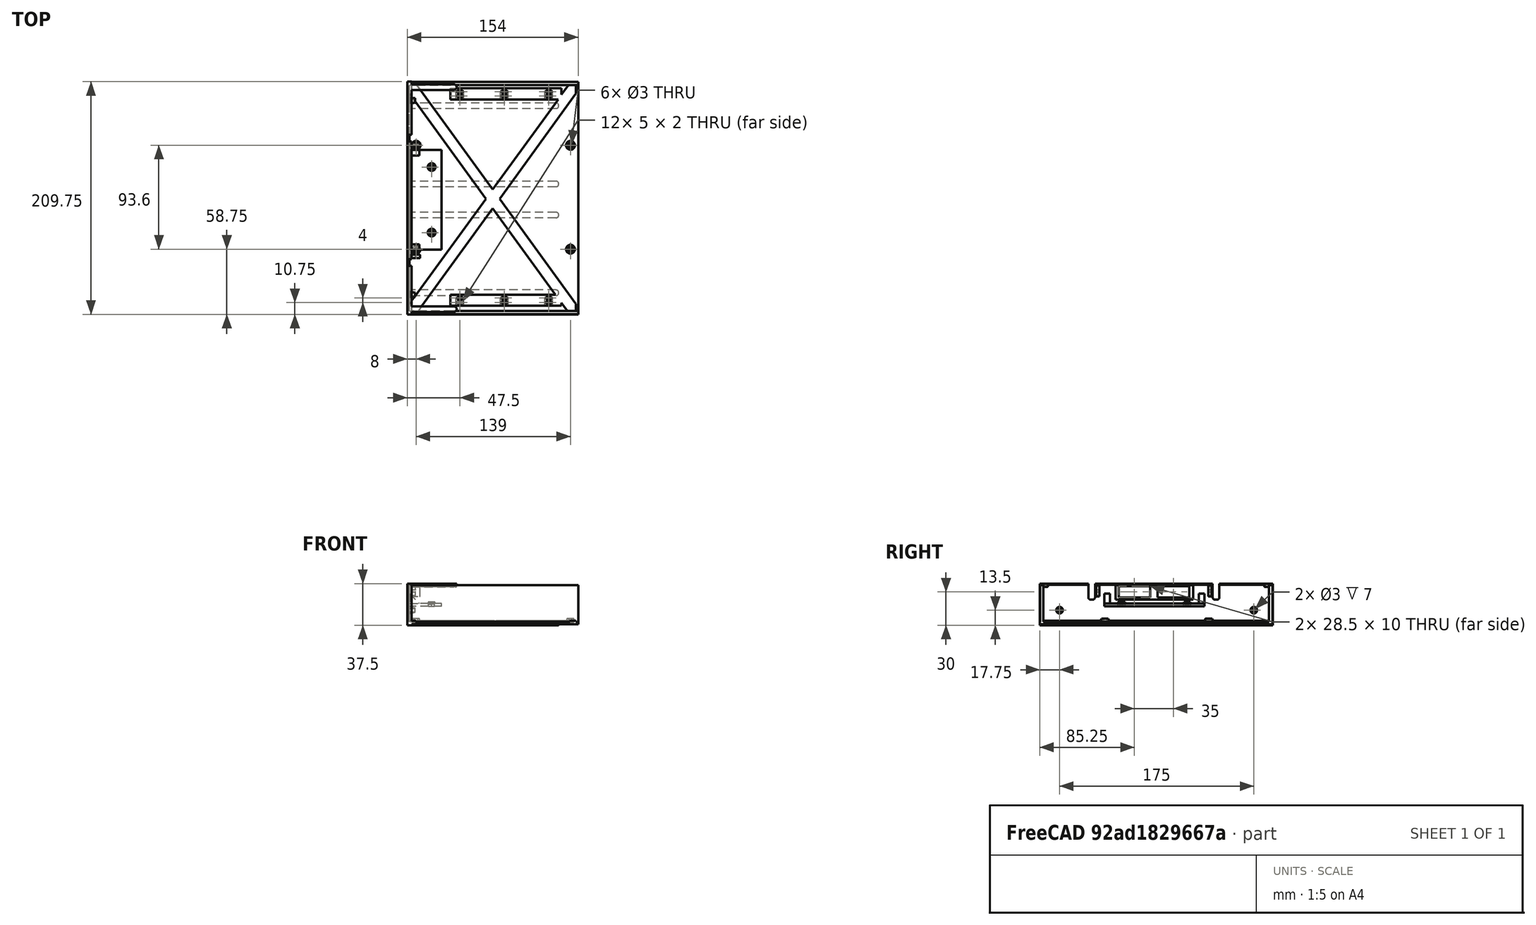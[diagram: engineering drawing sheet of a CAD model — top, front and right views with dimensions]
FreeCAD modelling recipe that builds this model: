
FCSTD DOCUMENT  (FreeCAD 0.19R24291 (Git))
Label: SBC61_tray_wider
License: All rights reserved
LicenseURL: http://en.wikipedia.org/wiki/All_rights_reserved
objects: Part::Box×69, Part::MultiFuse×39, Part::Cylinder×18, Part::Fillet×16, Part::Cut×12, Part::Cone×8, Part::MultiCommon×7, Mesh::Feature×3
note: 169 computed .brp shape members not serialized (recipe doc carries the construction recipe); baked Part::Feature solids carry a one-line shape summary decoded from their .brp

FEATURE [Part::Box] Box  label="Cube"
  AttacherType = Attacher::AttachEngine3D
  Height = 2
  Length = 150
  Placement = pos=(0,-54.75,0) rot=(0,0,1;0rad)
  Width = 209.25
FEATURE [Part::Cylinder] Cylinder
  Angle = 360
  AttacherType = Attacher::AttachEngine3D
  Height = 10
  Placement = pos=(4,4,-1) rot=(0,0,1;0rad)
  Radius = 1.5
FEATURE [Part::Box] Box001  label="Cube001"
  AttacherType = Attacher::AttachEngine3D
  Height = 37.5
  Length = 4
  Placement = pos=(-5,-19.25,-1) rot=(0,0,1;0rad)
  Width = 209.75
FEATURE [Part::Box] Box002  label="Cube002"
  AttacherType = Attacher::AttachEngine3D
  Height = 3
  Length = 130
  Placement = pos=(0,0.75,-2) rot=(0,0,1;0rad)
  Width = 5
FEATURE [Part::Fillet] Fillet
  Base = -> Box002
  Edges = 2 edges r=0.5: [Edge9,Edge11]
FEATURE [Part::Cylinder] Cylinder004
  Angle = 360
  AttacherType = Attacher::AttachEngine3D
  Height = 3
  Placement = pos=(130,3.25,-2) rot=(0,0,-1;0rad)
  Radius = 2.5
FEATURE [Part::Fillet] Fillet001
  Base = -> Cylinder004
  Edges = 1 edges r=0.5: [Edge3]
FEATURE [Part::MultiFuse] Fusion001
  Placement = pos=(0,-38.5,1) rot=(0,0,1;0rad)
  Shapes = -> [Fillet,Fillet001]
FEATURE [Part::Cylinder] Cylinder005
  Angle = 360
  AttacherType = Attacher::AttachEngine3D
  Height = 3
  Placement = pos=(130,3.25,-2) rot=(0,0,-1;0rad)
  Radius = 2.5
FEATURE [Part::Box] Box003  label="Cube003"
  AttacherType = Attacher::AttachEngine3D
  Height = 3
  Length = 130
  Placement = pos=(0,0.75,-2) rot=(0,0,1;0rad)
  Width = 5
FEATURE [Part::Fillet] Fillet002
  Base = -> Box003
  Edges = 2 edges r=0.5: [Edge9,Edge11]
FEATURE [Part::Fillet] Fillet003
  Base = -> Cylinder005
  Edges = 1 edges r=0.5: [Edge3]
FEATURE [Part::MultiFuse] Fusion002
  Placement = pos=(0,130,1) rot=(0,0,1;0rad)
  Shapes = -> [Fillet002,Fillet003]
FEATURE [Part::Cylinder] Cylinder006
  Angle = 360
  AttacherType = Attacher::AttachEngine3D
  Height = 3
  Placement = pos=(130,2.5,-2) rot=(0,0,-1;0rad)
  Radius = 2.5
FEATURE [Part::Box] Box004  label="Cube004"
  AttacherType = Attacher::AttachEngine3D
  Height = 3
  Length = 130
  Placement = pos=(0,0,-2) rot=(0,0,1;0rad)
  Width = 5
FEATURE [Part::Fillet] Fillet004
  Base = -> Box004
  Edges = 2 edges r=0.5: [Edge9,Edge11]
FEATURE [Part::Fillet] Fillet005
  Base = -> Cylinder006
  Edges = 1 edges r=0.5: [Edge3]
FEATURE [Part::MultiFuse] Fusion003
  Placement = pos=(0,60.25,1) rot=(0,0,1;0rad)
  Shapes = -> [Fillet004,Fillet005]
FEATURE [Part::Cylinder] Cylinder007
  Angle = 360
  AttacherType = Attacher::AttachEngine3D
  Height = 3
  Placement = pos=(130,2.5,-2) rot=(0,0,-1;0rad)
  Radius = 2.5
FEATURE [Part::Box] Box005  label="Cube005"
  AttacherType = Attacher::AttachEngine3D
  Height = 3
  Length = 130
  Placement = pos=(0,0,-2) rot=(0,0,1;0rad)
  Width = 5
FEATURE [Part::Fillet] Fillet006
  Base = -> Box005
  Edges = 2 edges r=0.5: [Edge9,Edge11]
FEATURE [Part::Fillet] Fillet007
  Base = -> Cylinder007
  Edges = 1 edges r=0.5: [Edge3]
FEATURE [Part::MultiFuse] Fusion004
  Placement = pos=(0,32.25,1) rot=(0,0,1;0rad)
  Shapes = -> [Fillet006,Fillet007]
FEATURE [Part::Box] Box006  label="Cube006"
  AttacherType = Attacher::AttachEngine3D
  Height = 35.2
  Length = 150
  Placement = pos=(0,-54.5,0) rot=(0,0,1;0rad)
  Width = 3
FEATURE [Part::Box] Box007  label="Cube007"
  AttacherType = Attacher::AttachEngine3D
  Height = 35.2
  Length = 150
  Placement = pos=(0,151.75,0) rot=(0,0,1;0rad)
  Width = 3
FEATURE [Part::Cylinder] Cylinder008
  Angle = 360
  AttacherType = Attacher::AttachEngine3D
  Height = 3
  Placement = pos=(38,3,-2) rot=(0,0,-1;0rad)
  Radius = 2.5
FEATURE [Part::Box] Box008  label="Cube008"
  AttacherType = Attacher::AttachEngine3D
  Height = 3
  Length = 38
  Placement = pos=(0,36.5,-2) rot=(0,0,1;0rad)
  Width = 5
FEATURE [Part::Fillet] Fillet008
  Base = -> Box008
  Edges = 2 edges r=0.5: [Edge9,Edge11]
  Placement = pos=(0,-36,0) rot=(0,0,1;0rad)
FEATURE [Part::Fillet] Fillet009
  Base = -> Cylinder008
  Edges = 1 edges r=0.5: [Edge3]
FEATURE [Part::MultiFuse] Fusion005
  Placement = pos=(0,-53,35.5) rot=(0,0,1;0rad)
  Shapes = -> [Fillet008,Fillet009]
FEATURE [Part::Cylinder] Cylinder009
  Angle = 360
  AttacherType = Attacher::AttachEngine3D
  Height = 3
  Placement = pos=(38,3,-2) rot=(0,0,-1;0rad)
  Radius = 2.5
FEATURE [Part::Box] Box009  label="Cube009"
  AttacherType = Attacher::AttachEngine3D
  Height = 3
  Length = 38
  Placement = pos=(0,0.5,-2) rot=(0,0,1;0rad)
  Width = 5
FEATURE [Part::Fillet] Fillet010
  Base = -> Box009
  Edges = 2 edges r=0.5: [Edge9,Edge11]
FEATURE [Part::Fillet] Fillet011
  Base = -> Cylinder009
  Edges = 1 edges r=0.5: [Edge3]
FEATURE [Part::MultiFuse] Fusion006
  Placement = pos=(0,147,35.5) rot=(0,0,1;0rad)
  Shapes = -> [Fillet010,Fillet011]
FEATURE [Part::Box] Box014  label="Cube014"
  AttacherType = Attacher::AttachEngine3D
  Height = 2
  Length = 5.45
  Placement = pos=(3.25,0,0) rot=(0,0,1;0rad)
  Width = 10
FEATURE [Part::Box] Box015  label="Cube015"
  AttacherType = Attacher::AttachEngine3D
  Height = 2
  Length = 5.45
  Placement = pos=(11.5,4,0) rot=(0,0,1;2.0944rad)
  Width = 10
FEATURE [Part::Box] Box016  label="Cube016"
  AttacherType = Attacher::AttachEngine3D
  Height = 2
  Length = 10
  Placement = pos=(0.55,4,0) rot=(0,0,-1;0.523599rad)
  Width = 5.45
FEATURE [Part::MultiCommon] Common  label="M.25 nut"
  Placement = pos=(-2,0,-1) rot=(0,0,1;0rad)
  Shapes = -> [Box014,Box016,Box015]
FEATURE [Part::Cone] Cone
  Angle = 360
  AttacherType = Attacher::AttachEngine3D
  Height = 3
  Placement = pos=(4,4,2) rot=(0,0,1;0rad)
  Radius1 = 4
  Radius2 = 3
FEATURE [Part::Cone] Cone001
  Angle = 360
  AttacherType = Attacher::AttachEngine3D
  Height = 3
  Placement = pos=(143,4,2) rot=(0,0,1;0rad)
  Radius1 = 4
  Radius2 = 3
FEATURE [Part::Cone] Cone002
  Angle = 360
  AttacherType = Attacher::AttachEngine3D
  Height = 3
  Placement = pos=(4,97.6,2) rot=(0,0,1;0rad)
  Radius1 = 4
  Radius2 = 3
FEATURE [Part::Cone] Cone003
  Angle = 360
  AttacherType = Attacher::AttachEngine3D
  Height = 3
  Placement = pos=(143,97.6,2) rot=(0,0,1;0rad)
  Radius1 = 4
  Radius2 = 3
FEATURE [Part::Box] Box017  label="Cube017"
  AttacherType = Attacher::AttachEngine3D
  Height = 33.5
  Length = 4
  Placement = pos=(-3,-16,2) rot=(0,0,1;0rad)
  Width = 203.25
FEATURE [Part::Cut] Cut  label="Face_plate_full"
  Base = -> Box001
  Placement = pos=(1,-34.5,0) rot=(0,0,1;0rad)
  Tool = -> Box017
FEATURE [Part::Box] Box018  label="Cube018"
  AttacherType = Attacher::AttachEngine3D
  Height = 15
  Length = 10
  Placement = pos=(0,0,16) rot=(0,0,1;0rad)
  Width = 6
FEATURE [Part::Fillet] Fillet012
  Base = -> Box018
  Edges = 2 edges r=2: [Edge9,Edge11]
  Placement = pos=(0,-10,4) rot=(0,0,1;0rad)
FEATURE [Part::Box] Box020  label="Cube020"
  AttacherType = Attacher::AttachEngine3D
  Height = 15
  Length = 10
  Placement = pos=(0,0,16) rot=(0,0,1;0rad)
  Width = 6
FEATURE [Part::Fillet] Fillet014
  Base = -> Box020
  Edges = 2 edges r=2: [Edge9,Edge11]
  Placement = pos=(0,102,4) rot=(0,0,1;0rad)
FEATURE [Part::MultiFuse] Fusion
  Placement = pos=(-5,0,2) rot=(0,0,1;0rad)
  Shapes = -> [Fillet012,Fillet014]
FEATURE [Part::Cut] Cut001  label="Face plate with cuts"
  Base = -> Cut
  Placement = pos=(0,-1,0) rot=(0,0,1;0rad)
  Tool = -> Fusion
FEATURE [Part::MultiFuse] Fusion007  label="Bottom"
  Shapes = -> [Box,Fusion001,Fusion002,Fusion003,Fusion004,Cone,Cone001,Cone002,Cone003]
FEATURE [Part::MultiFuse] Fusion008  label="screw_hole"
  Shapes = -> [Cylinder,Common]
FEATURE [Part::Box] Box021  label="Cube021"
  AttacherType = Attacher::AttachEngine3D
  Height = 2
  Length = 5.45
  Placement = pos=(3.25,0,0) rot=(0,0,1;0rad)
  Width = 10
FEATURE [Part::Box] Box022  label="Cube022"
  AttacherType = Attacher::AttachEngine3D
  Height = 2
  Length = 5.45
  Placement = pos=(11.5,4,0) rot=(0,0,1;2.0944rad)
  Width = 10
FEATURE [Part::Box] Box023  label="Cube023"
  AttacherType = Attacher::AttachEngine3D
  Height = 2
  Length = 10
  Placement = pos=(0.55,4,0) rot=(0,0,-1;0.523599rad)
  Width = 5.45
FEATURE [Part::Cylinder] Cylinder010
  Angle = 360
  AttacherType = Attacher::AttachEngine3D
  Height = 10
  Placement = pos=(4,4,-1) rot=(0,0,1;0rad)
  Radius = 1.5
FEATURE [Part::MultiCommon] Common001  label="M.25 nut001"
  Placement = pos=(-2,0,-1) rot=(0,0,1;0rad)
  Shapes = -> [Box021,Box023,Box022]
FEATURE [Part::MultiFuse] Fusion009  label="screw_hole001"
  Placement = pos=(139,0,0) rot=(0,0,1;0rad)
  Shapes = -> [Cylinder010,Common001]
FEATURE [Part::Box] Box024  label="Cube024"
  AttacherType = Attacher::AttachEngine3D
  Height = 2
  Length = 5.45
  Placement = pos=(3.25,0,0) rot=(0,0,1;0rad)
  Width = 10
FEATURE [Part::Box] Box025  label="Cube025"
  AttacherType = Attacher::AttachEngine3D
  Height = 2
  Length = 5.45
  Placement = pos=(11.5,4,0) rot=(0,0,1;2.0944rad)
  Width = 10
FEATURE [Part::Box] Box026  label="Cube026"
  AttacherType = Attacher::AttachEngine3D
  Height = 2
  Length = 10
  Placement = pos=(0.55,4,0) rot=(0,0,-1;0.523599rad)
  Width = 5.45
FEATURE [Part::Cylinder] Cylinder011
  Angle = 360
  AttacherType = Attacher::AttachEngine3D
  Height = 10
  Placement = pos=(4,4,-1) rot=(0,0,1;0rad)
  Radius = 1.5
FEATURE [Part::MultiCommon] Common002  label="M.25 nut002"
  Placement = pos=(-2,0,-1) rot=(0,0,1;0rad)
  Shapes = -> [Box024,Box026,Box025]
FEATURE [Part::MultiFuse] Fusion010  label="screw_hole002"
  Placement = pos=(0,93.6,0) rot=(0,0,1;0rad)
  Shapes = -> [Cylinder011,Common002]
FEATURE [Part::Box] Box027  label="Cube027"
  AttacherType = Attacher::AttachEngine3D
  Height = 2
  Length = 5.45
  Placement = pos=(3.25,0,0) rot=(0,0,1;0rad)
  Width = 10
FEATURE [Part::Box] Box028  label="Cube028"
  AttacherType = Attacher::AttachEngine3D
  Height = 2
  Length = 5.45
  Placement = pos=(11.5,4,0) rot=(0,0,1;2.0944rad)
  Width = 10
FEATURE [Part::Box] Box029  label="Cube029"
  AttacherType = Attacher::AttachEngine3D
  Height = 2
  Length = 10
  Placement = pos=(0.55,4,0) rot=(0,0,-1;0.523599rad)
  Width = 5.45
FEATURE [Part::Cylinder] Cylinder012
  Angle = 360
  AttacherType = Attacher::AttachEngine3D
  Height = 10
  Placement = pos=(4,4,-1) rot=(0,0,1;0rad)
  Radius = 1.5
FEATURE [Part::MultiCommon] Common003  label="M.25 nut003"
  Placement = pos=(-2,0,-1) rot=(0,0,1;0rad)
  Shapes = -> [Box027,Box029,Box028]
FEATURE [Part::MultiFuse] Fusion011  label="screw_hole003"
  Placement = pos=(139,93.6,0) rot=(0,0,1;0rad)
  Shapes = -> [Cylinder012,Common003]
FEATURE [Part::MultiFuse] Fusion012  label="Screws"
  Placement = pos=(0,0,0.5) rot=(0,0,1;0rad)
  Shapes = -> [Fusion008,Fusion009,Fusion010,Fusion011]
FEATURE [Part::Cut] Cut002
  Base = -> Fusion007
  Tool = -> Fusion012
FEATURE [Part::MultiFuse] Fusion013  label="SBC61_tray_whole"
  Shapes = -> [Fusion005,Fusion006,Box007,Box006,Cut001,Cut002]
FEATURE [Part::Cylinder] Cylinder003
  Angle = 360
  AttacherType = Attacher::AttachEngine3D
  Height = 10
  Placement = pos=(63,5,7) rot=(1,0,0;1.5708rad)
  Radius = 1.5
FEATURE [Part::Cylinder] Cylinder002
  Angle = 360
  AttacherType = Attacher::AttachEngine3D
  Height = 10
  Placement = pos=(38,5,7) rot=(1,0,0;1.5708rad)
  Radius = 1.5
FEATURE [Part::Cylinder] Cylinder001
  Angle = 360
  AttacherType = Attacher::AttachEngine3D
  Height = 10
  Placement = pos=(28,5,7) rot=(1,0,0;1.5708rad)
  Radius = 1.5
FEATURE [Part::Box] Box030  label="Cube030"
  AttacherType = Attacher::AttachEngine3D
  Height = 10
  Length = 28.5
  Placement = pos=(1.25,-1,2) rot=(0,0,1;0rad)
  Width = 10
FEATURE [Part::Cylinder] Cylinder013
  Angle = 360
  AttacherType = Attacher::AttachEngine3D
  Height = 10
  Placement = pos=(3,5,7) rot=(1,0,0;1.5708rad)
  Radius = 1.5
FEATURE [Part::Box] Box031  label="Cube031"
  AttacherType = Attacher::AttachEngine3D
  Height = 10
  Length = 28.5
  Placement = pos=(36.25,-1,2) rot=(0,0,1;0rad)
  Width = 10
FEATURE [Part::MultiFuse] Fusion015
  Shapes = -> [Cylinder013,Cylinder001,Cylinder002,Cylinder003]
FEATURE [Part::Box] Box032  label="Cube032"
  AttacherType = Attacher::AttachEngine3D
  Height = 13
  Length = 70
  Placement = pos=(-1.5,0,0) rot=(0,0,1;0rad)
  Width = 5
FEATURE [Part::MultiFuse] Fusion014  label="DB9s"
  Placement = pos=(2.5,15,22) rot=(0,0,1;1.5708rad)
  Shapes = -> [Cylinder003,Fusion015,Cylinder001,Cylinder002,Box032,Cylinder013,Box030,Box031]
FEATURE [Part::Cut] Cut003
  Base = -> Fusion013
  Tool = -> Fusion014
FEATURE [Part::Box] Box033  label="Cube033"
  AttacherType = Attacher::AttachEngine3D
  Height = 2.5
  Length = 90
  Placement = pos=(26.5,3.5,13) rot=(0,0,1;1.5708rad)
  Width = 30
FEATURE [Part::Cone] Cone004
  Angle = 360
  AttacherType = Attacher::AttachEngine3D
  Height = 3
  Placement = pos=(17.5,19,14) rot=(0,0,1;0rad)
  Radius1 = 4
  Radius2 = 3
FEATURE [Part::Cone] Cone005
  Angle = 360
  AttacherType = Attacher::AttachEngine3D
  Height = 3
  Placement = pos=(17.5,78,14) rot=(0,0,1;0rad)
  Radius1 = 4
  Radius2 = 3
FEATURE [Part::Box] Box034  label="Cube034"
  AttacherType = Attacher::AttachEngine3D
  Height = 10
  Length = 10
  Width = 5
FEATURE [Part::Box] Box035  label="Cube035"
  AttacherType = Attacher::AttachEngine3D
  Height = 20
  Length = 10
  Placement = pos=(0,0,0) rot=(0,1,0;0.785398rad)
  Width = 5
FEATURE [Part::Cut] Cut004
  Base = -> Box034
  Placement = pos=(-3.5,8.5,25.5) rot=(1,0,0;3.14159rad)
  Tool = -> Box035
FEATURE [Part::Box] Box036  label="Cube036"
  AttacherType = Attacher::AttachEngine3D
  Height = 20
  Length = 10
  Placement = pos=(0,0,0) rot=(0,1,0;0.785398rad)
  Width = 5
FEATURE [Part::Box] Box037  label="Cube037"
  AttacherType = Attacher::AttachEngine3D
  Height = 10
  Length = 10
  Width = 5
FEATURE [Part::Cut] Cut005
  Base = -> Box037
  Placement = pos=(-3.5,93.5,25.5) rot=(1,0,0;3.14159rad)
  Tool = -> Box036
FEATURE [Part::MultiFuse] Fusion016  label="CS863 board"
  Placement = pos=(0,0,-1) rot=(0,0,1;0rad)
  Shapes = -> [Box033,Cone004,Cone005,Cut004,Cut005]
FEATURE [Part::Box] Box038  label="Cube038"
  AttacherType = Attacher::AttachEngine3D
  Height = 2
  Length = 5.45
  Placement = pos=(3.25,0,0) rot=(0,0,1;0rad)
  Width = 10
FEATURE [Part::Box] Box039  label="Cube039"
  AttacherType = Attacher::AttachEngine3D
  Height = 2
  Length = 5.45
  Placement = pos=(11.5,4,0) rot=(0,0,1;2.0944rad)
  Width = 10
FEATURE [Part::Box] Box040  label="Cube040"
  AttacherType = Attacher::AttachEngine3D
  Height = 2
  Length = 10
  Placement = pos=(0.55,4,0) rot=(0,0,-1;0.523599rad)
  Width = 5.45
FEATURE [Part::Cylinder] Cylinder014
  Angle = 360
  AttacherType = Attacher::AttachEngine3D
  Height = 10
  Placement = pos=(4,4,-1) rot=(0,0,1;0rad)
  Radius = 1.5
FEATURE [Part::MultiCommon] Common004  label="M.25 nut004"
  Placement = pos=(-2,0,-1) rot=(0,0,1;0rad)
  Shapes = -> [Box038,Box040,Box039]
FEATURE [Part::MultiFuse] Fusion017  label="screw_hole004"
  Placement = pos=(13.5,15,13) rot=(0,0,1;0rad)
  Shapes = -> [Cylinder014,Common004]
FEATURE [Part::Box] Box041  label="Cube041"
  AttacherType = Attacher::AttachEngine3D
  Height = 2
  Length = 10
  Placement = pos=(0.55,4,0) rot=(0,0,-1;0.523599rad)
  Width = 5.45
FEATURE [Part::Cylinder] Cylinder015
  Angle = 360
  AttacherType = Attacher::AttachEngine3D
  Height = 10
  Placement = pos=(4,4,-1) rot=(0,0,1;0rad)
  Radius = 1.5
FEATURE [Part::Box] Box042  label="Cube042"
  AttacherType = Attacher::AttachEngine3D
  Height = 2
  Length = 5.45
  Placement = pos=(3.25,0,0) rot=(0,0,1;0rad)
  Width = 10
FEATURE [Part::Box] Box043  label="Cube043"
  AttacherType = Attacher::AttachEngine3D
  Height = 2
  Length = 5.45
  Placement = pos=(11.5,4,0) rot=(0,0,1;2.0944rad)
  Width = 10
FEATURE [Part::MultiCommon] Common005  label="M.25 nut005"
  Placement = pos=(-2,0,-1) rot=(0,0,1;0rad)
  Shapes = -> [Box042,Box041,Box043]
FEATURE [Part::MultiFuse] Fusion018  label="screw_hole005"
  Placement = pos=(13.5,74,13) rot=(0,0,1;0rad)
  Shapes = -> [Cylinder015,Common005]
FEATURE [Part::MultiFuse] Fusion019  label="CS863 screws"
  Shapes = -> [Fusion017,Fusion018]
FEATURE [Part::Cut] Cut006  label="CS863 support"
  Base = -> Fusion016
  Placement = pos=(0.5,0,4) rot=(0,0,1;0rad)
  Tool = -> Fusion019
FEATURE [Part::Box] Box044  label="Actual C61 board"
  AttacherType = Attacher::AttachEngine3D
  Height = 2
  Length = 147
  Placement = pos=(0,0,5) rot=(0,0,1;0rad)
  Width = 102
FEATURE [Part::MultiFuse] Fusion020  label="C61 tray001"
  Shapes = -> [Cut003,Cut006]
FEATURE [Part::Cut] Cut007  label="C61 tray"
  Base = -> Fusion020
  Tool = -> Box044
FEATURE [Part::Box] Box049  label="Cube048"
  AttacherType = Attacher::AttachEngine3D
  Height = 3
  Length = 3
  Placement = pos=(3,10,27) rot=(0,0,1;0rad)
  Width = 3
FEATURE [Part::Box] Box050  label="Cube049"
  AttacherType = Attacher::AttachEngine3D
  Height = 3
  Length = 3
  Placement = pos=(3,10,32) rot=(0,0,1;0rad)
  Width = 3
FEATURE [Part::MultiFuse] Fusion026
  Shapes = -> [Box049,Box050]
FEATURE [Part::Box] Box047  label="Cube046"
  AttacherType = Attacher::AttachEngine3D
  Height = 3
  Length = 3
  Placement = pos=(3,10,32) rot=(0,0,1;0rad)
  Width = 3
FEATURE [Part::Box] Box048  label="Cube047"
  AttacherType = Attacher::AttachEngine3D
  Height = 10
  Length = 10
  Placement = pos=(0,10,26) rot=(0,0,1;0rad)
  Width = 3
FEATURE [Part::Cut] Cut011
  Base = -> Box048
  Tool = -> Fusion026
FEATURE [Part::Fillet] Fillet023  label="zip ties holder001"
  Base = -> Cut011
  Edges = 22 edges r=0.2: [Edge5,Edge6,Edge7,Edge8,Edge9,Edge10,Edge11,Edge12,Edge13,Edge14,Edge15,Edge16,Edge19,Edge20,Edge21,Edge22,Edge23,Edge24,Edge25,Edge26,Edge27,Edge28]
  Placement = pos=(-1,87,-1) rot=(0,0,1;0rad)
FEATURE [Part::Box] Box045  label="Cube044"
  AttacherType = Attacher::AttachEngine3D
  Height = 10
  Length = 10
  Placement = pos=(0,10,26) rot=(0,0,1;0rad)
  Width = 3
FEATURE [Part::Box] Box046  label="Cube045"
  AttacherType = Attacher::AttachEngine3D
  Height = 3
  Length = 3
  Placement = pos=(3,10,27) rot=(0,0,1;0rad)
  Width = 3
FEATURE [Part::MultiFuse] Fusion025
  Shapes = -> [Box046,Box047]
FEATURE [Part::Cut] Cut010
  Base = -> Box045
  Tool = -> Fusion025
FEATURE [Part::Fillet] Fillet022  label="zip ties holder"
  Base = -> Cut010
  Edges = 22 edges r=0.2: [Edge5,Edge6,Edge7,Edge8,Edge9,Edge10,Edge11,Edge12,Edge13,Edge14,Edge15,Edge16,Edge19,Edge20,Edge21,Edge22,Edge23,Edge24,Edge25,Edge26,Edge27,Edge28]
  Placement = pos=(-1,-14,-1) rot=(0,0,1;0rad)
FEATURE [Part::MultiFuse] Fusion027  label="zip ties holders"
  Placement = pos=(-1.5,0,0) rot=(0,0,1;0rad)
  Shapes = -> [Fillet022,Fillet023]
FEATURE [Part::MultiFuse] Fusion028  label="C61 tray wider"
  Shapes = -> [Cut007,Fusion027]
FEATURE [Mesh::Feature] Rack___Middle_wider_Rack___Middle_Wider  label="Rack_-_Middle_wider-Rack - Middle Wider"
  Placement = pos=(0,256.25,-4) rot=(0,0,1;4.71239rad)
FEATURE [Part::Box] Box051  label="Cube050"
  AttacherType = Attacher::AttachEngine3D
  Height = 10
  Length = 7
  Width = 10
FEATURE [Part::Box] Box052  label="Cube051"
  AttacherType = Attacher::AttachEngine3D
  Height = 10
  Length = 5
  Placement = pos=(1,2,5) rot=(0,0,1;0rad)
  Width = 2
FEATURE [Part::Box] Box053  label="Cube052"
  AttacherType = Attacher::AttachEngine3D
  Height = 10
  Length = 5
  Placement = pos=(1,6,5) rot=(0,0,1;0rad)
  Width = 2
FEATURE [Part::MultiFuse] Fusion029  label="zip_cut"
  Placement = pos=(40,-47,-9) rot=(0,0,1;0rad)
  Shapes = -> [Box051,Box052,Box053]
FEATURE [Part::Box] Box054  label="Cube053"
  AttacherType = Attacher::AttachEngine3D
  Height = 10
  Length = 5
  Placement = pos=(1,2,5) rot=(0,0,1;0rad)
  Width = 2
FEATURE [Part::Box] Box055  label="Cube054"
  AttacherType = Attacher::AttachEngine3D
  Height = 10
  Length = 5
  Placement = pos=(1,6,5) rot=(0,0,1;0rad)
  Width = 2
FEATURE [Part::Box] Box056  label="Cube055"
  AttacherType = Attacher::AttachEngine3D
  Height = 10
  Length = 7
  Width = 10
FEATURE [Part::MultiFuse] Fusion030  label="zip_cut001"
  Placement = pos=(80,-47,-9) rot=(0,0,1;0rad)
  Shapes = -> [Box056,Box054,Box055]
FEATURE [Part::Box] Box057  label="Cube056"
  AttacherType = Attacher::AttachEngine3D
  Height = 10
  Length = 5
  Placement = pos=(1,2,5) rot=(0,0,1;0rad)
  Width = 2
FEATURE [Part::Box] Box058  label="Cube057"
  AttacherType = Attacher::AttachEngine3D
  Height = 10
  Length = 5
  Placement = pos=(1,6,5) rot=(0,0,1;0rad)
  Width = 2
FEATURE [Part::Box] Box059  label="Cube058"
  AttacherType = Attacher::AttachEngine3D
  Height = 10
  Length = 7
  Width = 10
FEATURE [Part::MultiFuse] Fusion031  label="zip_cut002"
  Placement = pos=(40,139,-9) rot=(0,0,1;0rad)
  Shapes = -> [Box059,Box057,Box058]
FEATURE [Part::Box] Box060  label="Cube059"
  AttacherType = Attacher::AttachEngine3D
  Height = 10
  Length = 5
  Placement = pos=(1,2,5) rot=(0,0,1;0rad)
  Width = 2
FEATURE [Part::Box] Box061  label="Cube060"
  AttacherType = Attacher::AttachEngine3D
  Height = 10
  Length = 5
  Placement = pos=(1,6,5) rot=(0,0,1;0rad)
  Width = 2
FEATURE [Part::Box] Box062  label="Cube061"
  AttacherType = Attacher::AttachEngine3D
  Height = 10
  Length = 7
  Width = 10
FEATURE [Part::MultiFuse] Fusion032  label="zip_cut003"
  Placement = pos=(80,139,-9) rot=(0,0,1;0rad)
  Shapes = -> [Box062,Box060,Box061]
FEATURE [Part::Box] Box063  label="Cube062"
  AttacherType = Attacher::AttachEngine3D
  Height = 10
  Length = 5
  Placement = pos=(1,2,5) rot=(0,0,1;0rad)
  Width = 2
FEATURE [Part::Box] Box064  label="Cube063"
  AttacherType = Attacher::AttachEngine3D
  Height = 10
  Length = 5
  Placement = pos=(1,6,5) rot=(0,0,1;0rad)
  Width = 2
FEATURE [Part::Box] Box065  label="Cube064"
  AttacherType = Attacher::AttachEngine3D
  Height = 10
  Length = 7
  Width = 10
FEATURE [Part::MultiFuse] Fusion033  label="zip_cut004"
  Placement = pos=(120,-47,-9) rot=(0,0,1;0rad)
  Shapes = -> [Box065,Box063,Box064]
FEATURE [Part::Box] Box066  label="Cube065"
  AttacherType = Attacher::AttachEngine3D
  Height = 10
  Length = 5
  Placement = pos=(1,2,5) rot=(0,0,1;0rad)
  Width = 2
FEATURE [Part::Box] Box067  label="Cube066"
  AttacherType = Attacher::AttachEngine3D
  Height = 10
  Length = 5
  Placement = pos=(1,6,5) rot=(0,0,1;0rad)
  Width = 2
FEATURE [Part::Box] Box068  label="Cube067"
  AttacherType = Attacher::AttachEngine3D
  Height = 10
  Length = 7
  Width = 10
FEATURE [Part::MultiFuse] Fusion034  label="zip_cut005"
  Placement = pos=(120,139,-9) rot=(0,0,1;0rad)
  Shapes = -> [Box068,Box066,Box067]
FEATURE [Part::MultiFuse] Fusion035  label="zip cuts"
  Shapes = -> [Fusion029,Fusion030,Fusion031,Fusion032,Fusion033,Fusion034]
FEATURE [Part::Box] Box069  label="Cube068"
  AttacherType = Attacher::AttachEngine3D
  Height = 2
  Length = 100
  Placement = pos=(35,-47,1) rot=(0,0,1;0rad)
  Width = 10
FEATURE [Part::Box] Box070  label="Cube069"
  AttacherType = Attacher::AttachEngine3D
  Height = 2
  Length = 100
  Placement = pos=(35,139,1) rot=(0,0,1;0rad)
  Width = 10
FEATURE [Part::MultiFuse] Fusion036
  Shapes = -> [Box069,Box070]
FEATURE [Part::MultiFuse] Fusion037
  Shapes = -> [Fusion036,Fusion028]
FEATURE [Part::Cut] Cut012  label="Fusion038"
  Base = -> Fusion037
  Placement = pos=(-185,0,0) rot=(0,0,1;0rad)
  Tool = -> Fusion035
FEATURE [Mesh::Feature] Rack___Middle_wider_Rack___Left_Side_shorter  label="Rack_-_Middle_wider-Rack - Left Side shorter"
  Placement = pos=(0,261,0) rot=(0,0,1;4.71239rad)
FEATURE [Mesh::Feature] Rack___Right_Side  label="Rack - Right Side"
  Placement = pos=(0,247,0) rot=(0,0,1;4.71239rad)
FEATURE [Part::Cylinder] Cylinder016
  Angle = 360
  AttacherType = Attacher::AttachEngine3D
  Height = 10
  Placement = pos=(-5,-37,32.5) rot=(0,1,0;1.5708rad)
  Radius = 1.5
FEATURE [Part::Cylinder] Cylinder017
  Angle = 360
  AttacherType = Attacher::AttachEngine3D
  Height = 10
  Placement = pos=(-5,138,32.5) rot=(0,1,0;1.5708rad)
  Radius = 1.5
FEATURE [Part::MultiFuse] Fusion023
  Placement = pos=(-186,0,-20) rot=(0,0,1;0rad)
  Shapes = -> [Cylinder016,Cylinder017]
FEATURE [Part::Cone] Cone006
  Angle = 360
  AttacherType = Attacher::AttachEngine3D
  Height = 5
  Placement = pos=(-1,-37,32.5) rot=(0,1,0;1.5708rad)
  Radius1 = 3
  Radius2 = 2
FEATURE [Part::Cone] Cone007
  Angle = 360
  AttacherType = Attacher::AttachEngine3D
  Height = 5
  Placement = pos=(-1,138,32.5) rot=(0,1,0;1.5708rad)
  Radius1 = 3
  Radius2 = 2
FEATURE [Part::MultiFuse] Fusion022
  Placement = pos=(-186,0,-20) rot=(0,0,1;0rad)
  Shapes = -> [Cone006,Cone007]
  expr: .Placement.Base.z = -20
FEATURE [Part::MultiFuse] Fusion038  label="Fusion039"
  Shapes = -> [Fusion022,Cut012]
FEATURE [Part::Cut] Cut013  label="SBC61 tray wider2"
  Base = -> Fusion038
  Tool = -> Fusion023
FEATURE [Part::Box] Box071  label="Cube070"
  AttacherType = Attacher::AttachEngine3D
  Height = 5
  Length = 300
  Placement = pos=(-202,-83,0) rot=(0,0,1;0.942478rad)
  Width = 10
FEATURE [Part::Box] Box072  label="Cube071"
  AttacherType = Attacher::AttachEngine3D
  Height = 5
  Length = 300
  Placement = pos=(-200,162,0) rot=(0,0,1;-0.942478rad)
  Width = 10
FEATURE [Part::Box] Box073  label="Cube072"
  AttacherType = Attacher::AttachEngine3D
  Height = 2
  Length = 150
  Placement = pos=(-187,-54.75,0) rot=(0,0,1;0rad)
  Width = 209.25
FEATURE [Part::MultiFuse] Fusion039  label="Fusion040"
  Shapes = -> [Box071,Box072]
FEATURE [Part::MultiCommon] Common006
  Placement = pos=(0,0,1) rot=(0,0,1;0rad)
  Shapes = -> [Box073,Fusion039]
FEATURE [Part::MultiFuse] Fusion040  label="SBC61 tray wider final"
  Shapes = -> [Cut013,Common006]
